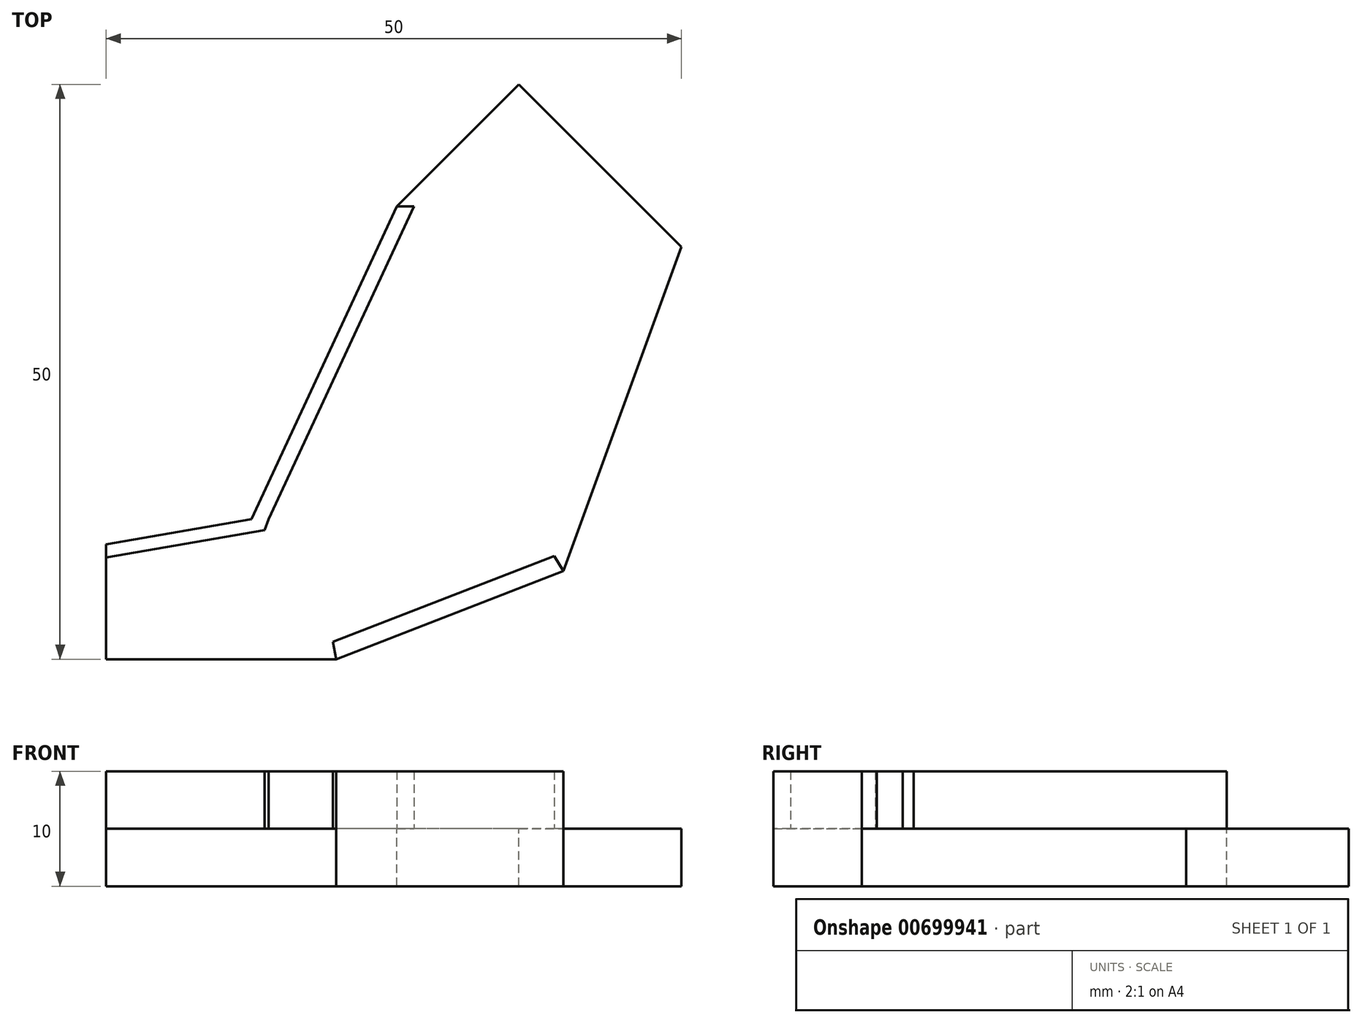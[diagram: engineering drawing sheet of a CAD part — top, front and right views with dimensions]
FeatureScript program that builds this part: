
annotation { "Feature Type Name" : "Feature", "Feature Type Description" : "" }
export const myFeature = defineFeature(function(context is Context, id is Id, definition is map)
    precondition{}
    {
        {
            var Q0;
            Q0=qCreatedBy(makeId("Top.planeOp"),FACE);
            var sketch = newSketch(context, id + "F0", { "sketchPlane" : qUnion([Q0])});
            skLineSegment(sketch, "E0.bottom", {"start": v(25, -25) * mm, "end": v(-25, -25) * mm});
            skLineSegment(sketch, "E0.top", {"start": v(25, 25) * mm, "end": v(-25, 25) * mm});
            skLineSegment(sketch, "E0.left", {"start": v(25, -25) * mm, "end": v(25, 25) * mm});
            skLineSegment(sketch, "E0.right", {"start": v(-25, -25) * mm, "end": v(-25, 25) * mm});
            skPoint(sketch, "E0.middle", {"position": v(0, 0) * mm});
            skSolve(sketch);
        }
        {
            var Q0;
            Q0=makeQuery(id+"F0.imprint","IMPRINT",FACE,{"disambiguationData":[TD([[makeQuery(id+"F0.imprint","IMPRINT",EDGE,{"derivedFrom":sQuery(id+"F0.wireOp",EDGE,"E0.bottom")}),-1.0]])]});
            extrude(context, id + "F1", {"entities" : qUnion([Q0]), "endBound" : BoundingType.SYMMETRIC, "depth" : 10 * mm, "offsetDistance" : 25 * mm});
        }
        {
            var Q0;
            Q0=makeQuery(id+"F1.opExtrude","CAP_FACE",FACE,{"disambiguationData":[OSD([sQuery(id+"F0.wireOp",EDGE,"E0.bottom"),sQuery(id+"F0.wireOp",EDGE,"E0.top"),sQuery(id+"F0.wireOp",EDGE,"E0.left"),sQuery(id+"F0.wireOp",EDGE,"E0.right")])],"isStart":false});
            var sketch = newSketch(context, id + "F2", { "sketchPlane" : qUnion([Q0])});
            skLineSegment(sketch, "E1", {"start": v(10.86, 25) * mm, "end": v(25, 10.86) * mm});
            skLineSegment(sketch, "E2", {"start": v(10.86, 25) * mm, "end": v(0.26, 14.38) * mm});
            skLineSegment(sketch, "E3", {"start": v(0.26, 14.38) * mm, "end": v(-12.39, -12.82) * mm});
            skLineSegment(sketch, "E4", {"start": v(25, 10.86) * mm, "end": v(14.74, -17.33) * mm});
            skLineSegment(sketch, "E5", {"start": v(-5, -25) * mm, "end": v(14.74, -17.33) * mm});
            skLineSegment(sketch, "E6", {"start": v(-12.39, -12.82) * mm, "end": v(-25, -15) * mm});
            skSolve(sketch);
        }
        {
            var Q0;
            {var subQ3=sQuery(id+"F2.wireOp",EDGE,"E2");Q0=makeQuery(id+"F2.imprint","IMPRINT",FACE,{"disambiguationData":[TD([[makeQuery(id+"F2.imprint","IMPRINT",EDGE,{"derivedFrom":subQ3}),-1.0]])]});}
            var Q1;
            {var subQ0=sQuery(id+"F2.wireOp",EDGE,"E4");Q1=makeQuery(id+"F2.imprint","IMPRINT",FACE,{"disambiguationData":[TD([[makeQuery(id+"F2.imprint","IMPRINT",EDGE,{"derivedFrom":subQ0}),1.0]])]});}
            var Q2;
            {var subQ0=sQuery(id+"F2.wireOp",EDGE,"E1");Q2=makeQuery(id+"F2.imprint","IMPRINT",FACE,{"disambiguationData":[TD([[makeQuery(id+"F2.imprint","IMPRINT",EDGE,{"derivedFrom":subQ0}),1.0]])]});}
            extrude(context, id + "F3", {"entities" : qUnion([Q0, Q1, Q2]), "operationType" : NewBodyOperationType.REMOVE, "oppositeDirection" : true, "depth" : 10 * mm, "offsetDistance" : 25 * mm});
        }
        {
            var Q0;
            Q0=makeQuery(id+"F1.opExtrude","CAP_FACE",FACE,{"disambiguationData":[OSD([sQuery(id+"F0.wireOp",EDGE,"E0.bottom"),sQuery(id+"F0.wireOp",EDGE,"E0.top"),sQuery(id+"F0.wireOp",EDGE,"E0.left"),sQuery(id+"F0.wireOp",EDGE,"E0.right")])],"isStart":false});
            extrude(context, id + "F4", {"entities" : qUnion([Q0]), "operationType" : NewBodyOperationType.REMOVE, "oppositeDirection" : true, "depth" : 5 * mm, "offsetDistance" : 25 * mm});
        }
        {
            var Q0;
            Q0=makeQuery(id+"F4.boolean.opBoolean","COPY",FACE,{"derivedFrom":makeQuery(id+"F4.opExtrude","CAP_FACE",FACE,{"disambiguationData":[OSD([sQuery(id+"F0.wireOp",EDGE,"E0.bottom"),sQuery(id+"F0.wireOp",EDGE,"E0.top"),sQuery(id+"F0.wireOp",EDGE,"E0.left"),sQuery(id+"F0.wireOp",EDGE,"E0.right")])],"isStart":false})});
            var sketch = newSketch(context, id + "F5", { "sketchPlane" : qUnion([Q0])});
            skLineSegment(sketch, "E7", {"start": v(10.1, 24.24) * mm, "end": v(24.6, 9.74) * mm});
            skLineSegment(sketch, "E8", {"start": v(24.6, 9.74) * mm, "end": v(23.67, 10.67) * mm});
            skLineSegment(sketch, "E9", {"start": v(23.67, 10.67) * mm, "end": v(13.95, -16.03) * mm});
            skLineSegment(sketch, "E10", {"start": v(14.74, -17.33) * mm, "end": v(13.95, -16.03) * mm});
            skLineSegment(sketch, "E11", {"start": v(13.95, -16.03) * mm, "end": v(-5.28, -23.5) * mm});
            skLineSegment(sketch, "E12", {"start": v(-5.28, -23.5) * mm, "end": v(-5, -25) * mm});
            skLineSegment(sketch, "E13", {"start": v(-5, -25) * mm, "end": v(-5.28, -23.5) * mm});
            skLineSegment(sketch, "E14", {"start": v(-25, -23.5) * mm, "end": v(-5.28, -23.5) * mm});
            skLineSegment(sketch, "E15", {"start": v(10.86, 23.48) * mm, "end": v(1.76, 14.38) * mm});
            skLineSegment(sketch, "E16", {"start": v(0.26, 14.38) * mm, "end": v(1.76, 14.38) * mm});
            skLineSegment(sketch, "E17", {"start": v(1.76, 14.38) * mm, "end": v(-10.89, -12.82) * mm});
            skLineSegment(sketch, "E18", {"start": v(-10.89, -12.82) * mm, "end": v(-12.39, -12.82) * mm});
            skLineSegment(sketch, "E19", {"start": v(-25, -16.14) * mm, "end": v(-11.22, -13.76) * mm});
            skLineSegment(sketch, "E20", {"start": v(-11.22, -13.76) * mm, "end": v(-12.39, -12.82) * mm});
            skLineSegment(sketch, "E21", {"start": v(-11.22, -13.76) * mm, "end": v(-10.89, -12.82) * mm});
            skSolve(sketch);
        }
        {
            var Q0;
            Q0 = qSketchRegion(id + "F5", true);
            var Q1;
            Q1=makeQuery(id+"F5.imprint","IMPRINT",FACE,{"disambiguationData":[TD([[makeQuery(id+"F5.imprint","IMPRINT",EDGE,{"derivedFrom":sQuery(id+"F5.wireOp",EDGE,"E16")}),-1.0]])]});
            var Q2;
            {var subQ0=sQuery(id+"F5.wireOp",EDGE,"E19");Q2=makeQuery(id+"F5.imprint","IMPRINT",FACE,{"disambiguationData":[TD([[makeQuery(id+"F5.imprint","IMPRINT",EDGE,{"derivedFrom":subQ0}),1.0]])]});}
            var Q3;
            Q3=makeQuery(id+"F5.imprint","IMPRINT",FACE,{"disambiguationData":[TD([[makeQuery(id+"F5.imprint","IMPRINT",EDGE,{"derivedFrom":sQuery(id+"F5.wireOp",EDGE,"E13")}),1.0]])]});
            var Q4;
            Q4=makeQuery(id+"F5.imprint","IMPRINT",FACE,{"disambiguationData":[TD([[makeQuery(id+"F5.imprint","IMPRINT",EDGE,{"derivedFrom":sQuery(id+"F5.wireOp",EDGE,"E10")}),1.0]])]});
            var Q5;
            {var subQ0=sQuery(id+"F5.wireOp",EDGE,"E8");Q5=makeQuery(id+"F5.imprint","IMPRINT",FACE,{"disambiguationData":[TD([[makeQuery(id+"F5.imprint","IMPRINT",EDGE,{"derivedFrom":subQ0}),1.0]])]});}
            var Q6;
            {var subQ0=sQuery(id+"F5.wireOp",EDGE,"E8");Q6=makeQuery(id+"F5.imprint","IMPRINT",FACE,{"disambiguationData":[TD([[makeQuery(id+"F5.imprint","IMPRINT",EDGE,{"derivedFrom":subQ0}),-1.0]])]});}
            extrude(context, id + "F6", {"entities" : qUnion([Q0, Q1, Q2, Q3, Q4, Q5, Q6]), "operationType" : NewBodyOperationType.ADD, "depth" : 5 * mm, "offsetDistance" : 25 * mm});
        }
    });
